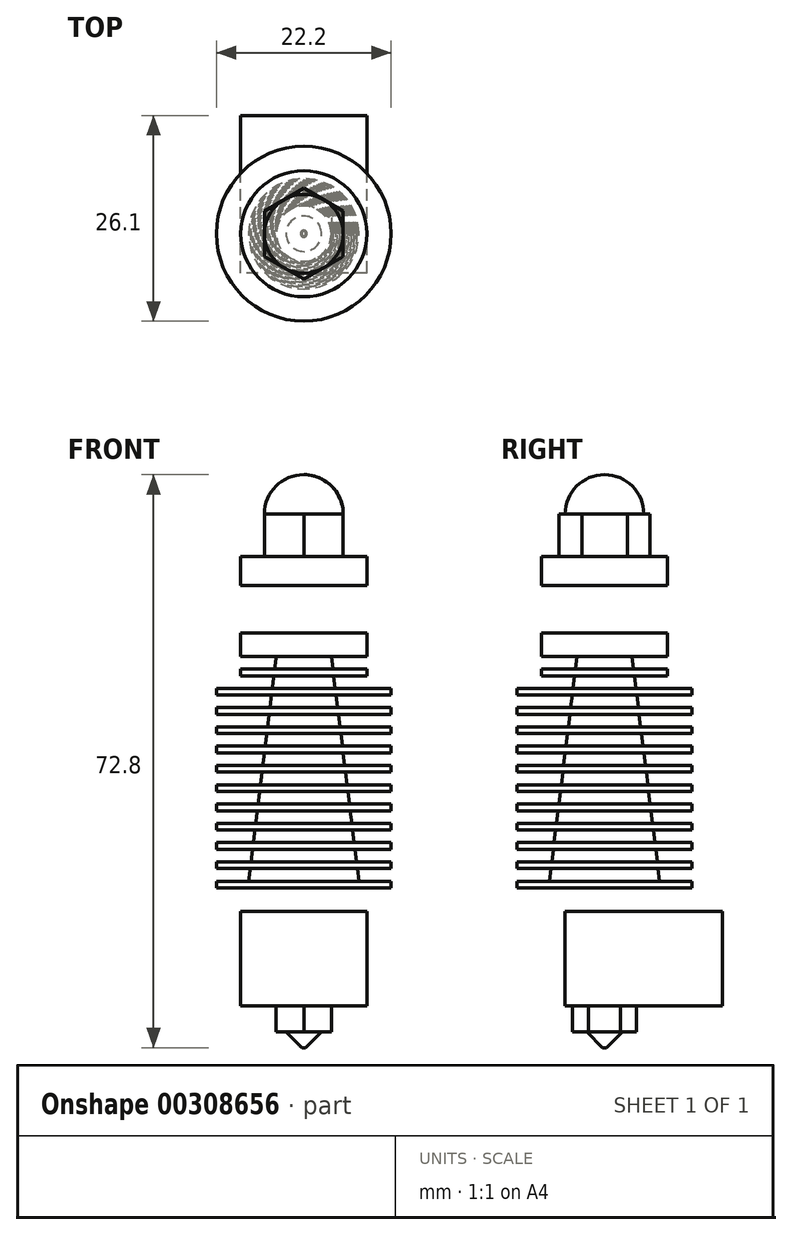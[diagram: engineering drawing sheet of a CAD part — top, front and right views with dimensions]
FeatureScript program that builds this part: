
annotation { "Feature Type Name" : "Feature", "Feature Type Description" : "" }
export const myFeature = defineFeature(function(context is Context, id is Id, definition is map)
    precondition{}
    {
        {
            var Q0;
            Q0=qCreatedBy(makeId("Front.planeOp"),FACE);
            var sketch = newSketch(context, id + "F0", { "sketchPlane" : qUnion([Q0])});
            skLineSegment(sketch, "E0.bottom", {"start": v(0, 0) * mm, "end": v(-11.1, 0) * mm});
            skLineSegment(sketch, "E0.top", {"start": v(0, -0.85) * mm, "end": v(-11.1, -0.85) * mm});
            skLineSegment(sketch, "E0.left", {"start": v(0, 0) * mm, "end": v(0, -0.85) * mm});
            skLineSegment(sketch, "E0.right", {"start": v(-11.1, 0) * mm, "end": v(-11.1, -0.85) * mm});
            skLineSegment(sketch, "E1.1.0.0", {"start": v(0, 1.6) * mm, "end": v(-11.1, 1.6) * mm});
            skLineSegment(sketch, "E1.1.0.1", {"start": v(-11.1, 2.45) * mm, "end": v(-11.1, 1.6) * mm});
            skLineSegment(sketch, "E1.1.0.2", {"start": v(0, 2.45) * mm, "end": v(-11.1, 2.45) * mm});
            skLineSegment(sketch, "E1.1.0.3", {"start": v(0, 2.45) * mm, "end": v(0, 1.6) * mm});
            skLineSegment(sketch, "E1.2.0.0", {"start": v(0, 4.05) * mm, "end": v(-11.1, 4.05) * mm});
            skLineSegment(sketch, "E1.2.0.1", {"start": v(-11.1, 4.9) * mm, "end": v(-11.1, 4.05) * mm});
            skLineSegment(sketch, "E1.2.0.2", {"start": v(0, 4.9) * mm, "end": v(-11.1, 4.9) * mm});
            skLineSegment(sketch, "E1.2.0.3", {"start": v(0, 4.9) * mm, "end": v(0, 4.05) * mm});
            skLineSegment(sketch, "E1.3.0.0", {"start": v(0, 6.5) * mm, "end": v(-11.1, 6.5) * mm});
            skLineSegment(sketch, "E1.3.0.1", {"start": v(-11.1, 7.35) * mm, "end": v(-11.1, 6.5) * mm});
            skLineSegment(sketch, "E1.3.0.2", {"start": v(0, 7.35) * mm, "end": v(-11.1, 7.35) * mm});
            skLineSegment(sketch, "E1.3.0.3", {"start": v(0, 7.35) * mm, "end": v(0, 6.5) * mm});
            skLineSegment(sketch, "E1.4.0.0", {"start": v(0, 8.95) * mm, "end": v(-11.1, 8.95) * mm});
            skLineSegment(sketch, "E1.4.0.1", {"start": v(-11.1, 9.8) * mm, "end": v(-11.1, 8.95) * mm});
            skLineSegment(sketch, "E1.4.0.2", {"start": v(0, 9.8) * mm, "end": v(-11.1, 9.8) * mm});
            skLineSegment(sketch, "E1.4.0.3", {"start": v(0, 9.8) * mm, "end": v(0, 8.95) * mm});
            skLineSegment(sketch, "E1.5.0.0", {"start": v(0, 11.4) * mm, "end": v(-11.1, 11.4) * mm});
            skLineSegment(sketch, "E1.5.0.1", {"start": v(-11.1, 12.25) * mm, "end": v(-11.1, 11.4) * mm});
            skLineSegment(sketch, "E1.5.0.2", {"start": v(0, 12.25) * mm, "end": v(-11.1, 12.25) * mm});
            skLineSegment(sketch, "E1.5.0.3", {"start": v(0, 12.25) * mm, "end": v(0, 11.4) * mm});
            skLineSegment(sketch, "E1.6.0.0", {"start": v(0, 13.85) * mm, "end": v(-11.1, 13.85) * mm});
            skLineSegment(sketch, "E1.6.0.1", {"start": v(-11.1, 14.7) * mm, "end": v(-11.1, 13.85) * mm});
            skLineSegment(sketch, "E1.6.0.2", {"start": v(0, 14.7) * mm, "end": v(-11.1, 14.7) * mm});
            skLineSegment(sketch, "E1.6.0.3", {"start": v(0, 14.7) * mm, "end": v(0, 13.85) * mm});
            skLineSegment(sketch, "E1.7.0.0", {"start": v(0, 16.3) * mm, "end": v(-11.1, 16.3) * mm});
            skLineSegment(sketch, "E1.7.0.1", {"start": v(-11.1, 17.15) * mm, "end": v(-11.1, 16.3) * mm});
            skLineSegment(sketch, "E1.7.0.2", {"start": v(0, 17.15) * mm, "end": v(-11.1, 17.15) * mm});
            skLineSegment(sketch, "E1.7.0.3", {"start": v(0, 17.15) * mm, "end": v(0, 16.3) * mm});
            skLineSegment(sketch, "E1.8.0.0", {"start": v(0, 18.75) * mm, "end": v(-11.1, 18.75) * mm});
            skLineSegment(sketch, "E1.8.0.1", {"start": v(-11.1, 19.6) * mm, "end": v(-11.1, 18.75) * mm});
            skLineSegment(sketch, "E1.8.0.2", {"start": v(0, 19.6) * mm, "end": v(-11.1, 19.6) * mm});
            skLineSegment(sketch, "E1.8.0.3", {"start": v(0, 19.6) * mm, "end": v(0, 18.75) * mm});
            skLineSegment(sketch, "E1.9.0.0", {"start": v(0, 21.2) * mm, "end": v(-11.1, 21.2) * mm});
            skLineSegment(sketch, "E1.9.0.1", {"start": v(-11.1, 22.05) * mm, "end": v(-11.1, 21.2) * mm});
            skLineSegment(sketch, "E1.9.0.2", {"start": v(0, 22.05) * mm, "end": v(-11.1, 22.05) * mm});
            skLineSegment(sketch, "E1.9.0.3", {"start": v(0, 22.05) * mm, "end": v(0, 21.2) * mm});
            skLineSegment(sketch, "E1.10.0.0", {"start": v(0, 23.65) * mm, "end": v(-11.1, 23.65) * mm});
            skLineSegment(sketch, "E1.10.0.1", {"start": v(-11.1, 24.5) * mm, "end": v(-11.1, 23.65) * mm});
            skLineSegment(sketch, "E1.10.0.2", {"start": v(0, 24.5) * mm, "end": v(-11.1, 24.5) * mm});
            skLineSegment(sketch, "E1.10.0.3", {"start": v(0, 24.5) * mm, "end": v(0, 23.65) * mm});
            skLineSegment(sketch, "E1.direction1", {"start": v(-11.1, -0.85) * mm, "end": v(-11.1, 1.6) * mm, "construction": true});
            skLineSegment(sketch, "E2.bottom", {"start": v(0, 26.95) * mm, "end": v(-8, 26.95) * mm});
            skLineSegment(sketch, "E2.top", {"start": v(0, 26.1) * mm, "end": v(-8, 26.1) * mm});
            skLineSegment(sketch, "E2.left", {"start": v(0, 26.95) * mm, "end": v(0, 26.1) * mm});
            skLineSegment(sketch, "E2.right", {"start": v(-8, 26.95) * mm, "end": v(-8, 26.1) * mm});
            skLineSegment(sketch, "E3.bottom", {"start": v(0, 31.55) * mm, "end": v(-8, 31.55) * mm});
            skLineSegment(sketch, "E3.top", {"start": v(0, 28.55) * mm, "end": v(-8, 28.55) * mm});
            skLineSegment(sketch, "E3.left", {"start": v(0, 31.55) * mm, "end": v(0, 28.55) * mm});
            skLineSegment(sketch, "E3.right", {"start": v(-8, 31.55) * mm, "end": v(-8, 28.55) * mm});
            skLineSegment(sketch, "E4.bottom", {"start": v(0, 31.55) * mm, "end": v(-6, 31.55) * mm});
            skLineSegment(sketch, "E4.top", {"start": v(0, 37.55) * mm, "end": v(-6, 37.55) * mm});
            skLineSegment(sketch, "E4.left", {"start": v(0, 31.55) * mm, "end": v(0, 37.55) * mm});
            skLineSegment(sketch, "E4.right", {"start": v(-6, 31.55) * mm, "end": v(-6, 37.55) * mm});
            skLineSegment(sketch, "E5.bottom", {"start": v(0, 37.55) * mm, "end": v(-8, 37.55) * mm});
            skLineSegment(sketch, "E5.top", {"start": v(0, 41.25) * mm, "end": v(-8, 41.25) * mm});
            skLineSegment(sketch, "E5.left", {"start": v(0, 37.55) * mm, "end": v(0, 41.25) * mm});
            skLineSegment(sketch, "E5.right", {"start": v(-8, 37.55) * mm, "end": v(-8, 41.25) * mm});
            skLineSegment(sketch, "E6", {"start": v(-3.5, 28.55) * mm, "end": v(-7, 0) * mm});
            skLineSegment(sketch, "E7", {"start": v(0, 28.55) * mm, "end": v(0, -0.85) * mm});
            skArc(sketch, "E8", {"start": v(-0.43, 31.55) * mm, "mid": v(-0.22, 31.5) * mm, "end": v(0, 31.45) * mm});
            skArc(sketch, "E9", {"start": v(0, 51.65) * mm, "mid": v(-3.54, 50.19) * mm, "end": v(-5, 46.65) * mm});
            skLineSegment(sketch, "E10", {"start": v(0, 46.65) * mm, "end": v(-5, 46.65) * mm});
            skLineSegment(sketch, "E11", {"start": v(0, 46.65) * mm, "end": v(0, 51.65) * mm});
            skLineSegment(sketch, "E12.bottom", {"start": v(0, -0.85) * mm, "end": v(-2.5, -0.85) * mm});
            skLineSegment(sketch, "E12.top", {"start": v(0, -3.85) * mm, "end": v(-2.5, -3.85) * mm});
            skLineSegment(sketch, "E12.left", {"start": v(0, -0.85) * mm, "end": v(0, -3.85) * mm});
            skLineSegment(sketch, "E12.right", {"start": v(-2.5, -0.85) * mm, "end": v(-2.5, -3.85) * mm});
            skLineSegment(sketch, "E13.bottom", {"start": v(0, -3.85) * mm, "end": v(-8, -3.85) * mm});
            skLineSegment(sketch, "E13.top", {"start": v(0, -15.85) * mm, "end": v(-8, -15.85) * mm});
            skLineSegment(sketch, "E13.left", {"start": v(0, -3.85) * mm, "end": v(0, -15.85) * mm});
            skLineSegment(sketch, "E13.right", {"start": v(-8, -3.85) * mm, "end": v(-8, -15.85) * mm});
            skLineSegment(sketch, "E14.MirrorCS", {"start": v(0, -15.85) * mm, "end": v(8, -15.85) * mm});
            skLineSegment(sketch, "E15.MirrorCS", {"start": v(8, -3.85) * mm, "end": v(8, -15.85) * mm});
            skLineSegment(sketch, "E16.MirrorCS", {"start": v(0, -3.85) * mm, "end": v(8, -3.85) * mm});
            skSolve(sketch);
        }
        {
            var Q0;
            Q0=makeQuery(id+"F0.imprint","IMPRINT",FACE,{"disambiguationData":[TD([[makeQuery(id+"F0.imprint","IMPRINT",EDGE,{"derivedFrom":sQuery(id+"F0.wireOp",EDGE,"E5.top")}),1.0]])]});
            var Q1;
            Q1=makeQuery(id+"F0.imprint","IMPRINT",FACE,{"disambiguationData":[TD([[makeQuery(id+"F0.imprint","IMPRINT",EDGE,{"derivedFrom":sQuery(id+"F0.wireOp",EDGE,"E4.bottom")}),-1.0]])]});
            var Q2;
            Q2=makeQuery(id+"F0.imprint","IMPRINT",FACE,{"disambiguationData":[TD([[makeQuery(id+"F0.imprint","IMPRINT",EDGE,{"derivedFrom":sQuery(id+"F0.wireOp",EDGE,"E3.bottom")}),1.0]])]});
            var Q3;
            {var subQ0=sQuery(id+"F0.wireOp",EDGE,"E7");var subQ1=sQuery(id+"F0.wireOp",EDGE,"E2.bottom");var subQ2=makeQuery(id+"F0.imprint","INTERSECT",VERTEX,{"derivedFrom":[subQ1,subQ0]});Q3=makeQuery(id+"F0.imprint","IMPRINT",FACE,{"disambiguationData":[TD([[makeQuery(id+"F0.imprint","IMPRINT",EDGE,{"disambiguationData":[TD([[subQ2,-1.0]])],"derivedFrom":subQ1}),-1.0]])]});}
            var Q4;
            {var subQ0=sQuery(id+"F0.wireOp",EDGE,"E7");var subQ1=sQuery(id+"F0.wireOp",EDGE,"E1.6.0.0");var subQ2=makeQuery(id+"F0.imprint","INTERSECT",VERTEX,{"derivedFrom":[subQ1,subQ0]});Q4=makeQuery(id+"F0.imprint","IMPRINT",FACE,{"disambiguationData":[TD([[makeQuery(id+"F0.imprint","IMPRINT",EDGE,{"disambiguationData":[TD([[subQ2,-1.0]])],"derivedFrom":subQ1}),-1.0]])]});}
            var Q5;
            {var subQ1=sQuery(id+"F0.wireOp",EDGE,"E0.top");Q5=makeQuery(id+"F0.imprint","IMPRINT",FACE,{"disambiguationData":[TD([[makeQuery(id+"F0.imprint","IMPRINT",EDGE,{"derivedFrom":subQ1}),-1.0]])]});}
            var Q6;
            {var subQ0=sQuery(id+"F0.wireOp",EDGE,"E7");var subQ1=sQuery(id+"F0.wireOp",EDGE,"E1.1.0.0");var subQ2=makeQuery(id+"F0.imprint","INTERSECT",VERTEX,{"derivedFrom":[subQ1,subQ0]});Q6=makeQuery(id+"F0.imprint","IMPRINT",FACE,{"disambiguationData":[TD([[makeQuery(id+"F0.imprint","IMPRINT",EDGE,{"disambiguationData":[TD([[subQ2,-1.0]])],"derivedFrom":subQ1}),-1.0]])]});}
            var Q7;
            {var subQ0=sQuery(id+"F0.wireOp",EDGE,"E7");var subQ1=sQuery(id+"F0.wireOp",EDGE,"E1.8.0.2");var subQ2=makeQuery(id+"F0.imprint","INTERSECT",VERTEX,{"derivedFrom":[subQ1,subQ0]});Q7=makeQuery(id+"F0.imprint","IMPRINT",FACE,{"disambiguationData":[TD([[makeQuery(id+"F0.imprint","IMPRINT",EDGE,{"disambiguationData":[TD([[subQ2,-1.0]])],"derivedFrom":subQ1}),-1.0]])]});}
            var Q8;
            {var subQ0=sQuery(id+"F0.wireOp",EDGE,"E7");var subQ1=sQuery(id+"F0.wireOp",EDGE,"E2.bottom");var subQ2=makeQuery(id+"F0.imprint","INTERSECT",VERTEX,{"derivedFrom":[subQ1,subQ0]});Q8=makeQuery(id+"F0.imprint","IMPRINT",FACE,{"disambiguationData":[TD([[makeQuery(id+"F0.imprint","IMPRINT",EDGE,{"disambiguationData":[TD([[subQ2,-1.0]])],"derivedFrom":subQ1}),1.0]])]});}
            var Q9;
            {var subQ0=sQuery(id+"F0.wireOp",EDGE,"E7");var subQ1=sQuery(id+"F0.wireOp",EDGE,"E1.4.0.0");var subQ2=makeQuery(id+"F0.imprint","INTERSECT",VERTEX,{"derivedFrom":[subQ1,subQ0]});Q9=makeQuery(id+"F0.imprint","IMPRINT",FACE,{"disambiguationData":[TD([[makeQuery(id+"F0.imprint","IMPRINT",EDGE,{"disambiguationData":[TD([[subQ2,-1.0]])],"derivedFrom":subQ1}),-1.0]])]});}
            var Q10;
            {var subQ0=sQuery(id+"F0.wireOp",EDGE,"E7");var subQ1=sQuery(id+"F0.wireOp",EDGE,"E1.2.0.0");var subQ2=makeQuery(id+"F0.imprint","INTERSECT",VERTEX,{"derivedFrom":[subQ1,subQ0]});Q10=makeQuery(id+"F0.imprint","IMPRINT",FACE,{"disambiguationData":[TD([[makeQuery(id+"F0.imprint","IMPRINT",EDGE,{"disambiguationData":[TD([[subQ2,-1.0]])],"derivedFrom":subQ1}),-1.0]])]});}
            var Q11;
            {var subQ0=sQuery(id+"F0.wireOp",EDGE,"E7");var subQ1=sQuery(id+"F0.wireOp",EDGE,"E1.10.0.2");var subQ2=makeQuery(id+"F0.imprint","INTERSECT",VERTEX,{"derivedFrom":[subQ1,subQ0]});Q11=makeQuery(id+"F0.imprint","IMPRINT",FACE,{"disambiguationData":[TD([[makeQuery(id+"F0.imprint","IMPRINT",EDGE,{"disambiguationData":[TD([[subQ2,-1.0]])],"derivedFrom":subQ1}),-1.0]])]});}
            var Q12;
            {var subQ0=sQuery(id+"F0.wireOp",EDGE,"E7");var subQ1=sQuery(id+"F0.wireOp",EDGE,"E1.4.0.2");var subQ2=makeQuery(id+"F0.imprint","INTERSECT",VERTEX,{"derivedFrom":[subQ1,subQ0]});Q12=makeQuery(id+"F0.imprint","IMPRINT",FACE,{"disambiguationData":[TD([[makeQuery(id+"F0.imprint","IMPRINT",EDGE,{"disambiguationData":[TD([[subQ2,-1.0]])],"derivedFrom":subQ1}),-1.0]])]});}
            var Q13;
            {var subQ0=sQuery(id+"F0.wireOp",EDGE,"E7");var subQ1=sQuery(id+"F0.wireOp",EDGE,"E1.7.0.0");var subQ2=makeQuery(id+"F0.imprint","INTERSECT",VERTEX,{"derivedFrom":[subQ1,subQ0]});Q13=makeQuery(id+"F0.imprint","IMPRINT",FACE,{"disambiguationData":[TD([[makeQuery(id+"F0.imprint","IMPRINT",EDGE,{"disambiguationData":[TD([[subQ2,-1.0]])],"derivedFrom":subQ1}),-1.0]])]});}
            var Q14;
            {var subQ0=sQuery(id+"F0.wireOp",EDGE,"E7");var subQ1=sQuery(id+"F0.wireOp",EDGE,"E1.10.0.0");var subQ2=makeQuery(id+"F0.imprint","INTERSECT",VERTEX,{"derivedFrom":[subQ1,subQ0]});Q14=makeQuery(id+"F0.imprint","IMPRINT",FACE,{"disambiguationData":[TD([[makeQuery(id+"F0.imprint","IMPRINT",EDGE,{"disambiguationData":[TD([[subQ2,-1.0]])],"derivedFrom":subQ1}),-1.0]])]});}
            var Q15;
            {var subQ0=sQuery(id+"F0.wireOp",EDGE,"E7");var subQ1=sQuery(id+"F0.wireOp",EDGE,"E1.3.0.0");var subQ2=makeQuery(id+"F0.imprint","INTERSECT",VERTEX,{"derivedFrom":[subQ1,subQ0]});Q15=makeQuery(id+"F0.imprint","IMPRINT",FACE,{"disambiguationData":[TD([[makeQuery(id+"F0.imprint","IMPRINT",EDGE,{"disambiguationData":[TD([[subQ2,-1.0]])],"derivedFrom":subQ1}),-1.0]])]});}
            var Q16;
            {var subQ0=sQuery(id+"F0.wireOp",EDGE,"E7");var subQ1=sQuery(id+"F0.wireOp",EDGE,"E1.3.0.2");var subQ2=makeQuery(id+"F0.imprint","INTERSECT",VERTEX,{"derivedFrom":[subQ1,subQ0]});Q16=makeQuery(id+"F0.imprint","IMPRINT",FACE,{"disambiguationData":[TD([[makeQuery(id+"F0.imprint","IMPRINT",EDGE,{"disambiguationData":[TD([[subQ2,-1.0]])],"derivedFrom":subQ1}),-1.0]])]});}
            var Q17;
            {var subQ0=sQuery(id+"F0.wireOp",EDGE,"E7");var subQ1=sQuery(id+"F0.wireOp",EDGE,"E1.1.0.2");var subQ2=makeQuery(id+"F0.imprint","INTERSECT",VERTEX,{"derivedFrom":[subQ1,subQ0]});Q17=makeQuery(id+"F0.imprint","IMPRINT",FACE,{"disambiguationData":[TD([[makeQuery(id+"F0.imprint","IMPRINT",EDGE,{"disambiguationData":[TD([[subQ2,-1.0]])],"derivedFrom":subQ1}),-1.0]])]});}
            var Q18;
            {var subQ0=sQuery(id+"F0.wireOp",EDGE,"E7");var subQ1=sQuery(id+"F0.wireOp",EDGE,"E0.bottom");var subQ2=makeQuery(id+"F0.imprint","INTERSECT",VERTEX,{"derivedFrom":[subQ1,subQ0]});Q18=makeQuery(id+"F0.imprint","IMPRINT",FACE,{"disambiguationData":[TD([[makeQuery(id+"F0.imprint","IMPRINT",EDGE,{"disambiguationData":[TD([[subQ2,-1.0]])],"derivedFrom":subQ1}),-1.0]])]});}
            var Q19;
            {var subQ0=sQuery(id+"F0.wireOp",EDGE,"E7");var subQ1=sQuery(id+"F0.wireOp",EDGE,"E1.2.0.2");var subQ2=makeQuery(id+"F0.imprint","INTERSECT",VERTEX,{"derivedFrom":[subQ1,subQ0]});Q19=makeQuery(id+"F0.imprint","IMPRINT",FACE,{"disambiguationData":[TD([[makeQuery(id+"F0.imprint","IMPRINT",EDGE,{"disambiguationData":[TD([[subQ2,-1.0]])],"derivedFrom":subQ1}),-1.0]])]});}
            var Q20;
            {var subQ0=sQuery(id+"F0.wireOp",EDGE,"E7");var subQ1=sQuery(id+"F0.wireOp",EDGE,"E1.7.0.2");var subQ2=makeQuery(id+"F0.imprint","INTERSECT",VERTEX,{"derivedFrom":[subQ1,subQ0]});Q20=makeQuery(id+"F0.imprint","IMPRINT",FACE,{"disambiguationData":[TD([[makeQuery(id+"F0.imprint","IMPRINT",EDGE,{"disambiguationData":[TD([[subQ2,-1.0]])],"derivedFrom":subQ1}),-1.0]])]});}
            var Q21;
            {var subQ0=sQuery(id+"F0.wireOp",EDGE,"E7");var subQ1=sQuery(id+"F0.wireOp",EDGE,"E1.9.0.2");var subQ2=makeQuery(id+"F0.imprint","INTERSECT",VERTEX,{"derivedFrom":[subQ1,subQ0]});Q21=makeQuery(id+"F0.imprint","IMPRINT",FACE,{"disambiguationData":[TD([[makeQuery(id+"F0.imprint","IMPRINT",EDGE,{"disambiguationData":[TD([[subQ2,-1.0]])],"derivedFrom":subQ1}),-1.0]])]});}
            var Q22;
            {var subQ0=sQuery(id+"F0.wireOp",EDGE,"E7");var subQ1=sQuery(id+"F0.wireOp",EDGE,"E1.5.0.2");var subQ2=makeQuery(id+"F0.imprint","INTERSECT",VERTEX,{"derivedFrom":[subQ1,subQ0]});Q22=makeQuery(id+"F0.imprint","IMPRINT",FACE,{"disambiguationData":[TD([[makeQuery(id+"F0.imprint","IMPRINT",EDGE,{"disambiguationData":[TD([[subQ2,-1.0]])],"derivedFrom":subQ1}),-1.0]])]});}
            var Q23;
            {var subQ0=sQuery(id+"F0.wireOp",EDGE,"E7");var subQ1=sQuery(id+"F0.wireOp",EDGE,"E1.8.0.0");var subQ2=makeQuery(id+"F0.imprint","INTERSECT",VERTEX,{"derivedFrom":[subQ1,subQ0]});Q23=makeQuery(id+"F0.imprint","IMPRINT",FACE,{"disambiguationData":[TD([[makeQuery(id+"F0.imprint","IMPRINT",EDGE,{"disambiguationData":[TD([[subQ2,-1.0]])],"derivedFrom":subQ1}),-1.0]])]});}
            var Q24;
            {var subQ0=sQuery(id+"F0.wireOp",EDGE,"E7");var subQ1=sQuery(id+"F0.wireOp",EDGE,"E1.9.0.0");var subQ2=makeQuery(id+"F0.imprint","INTERSECT",VERTEX,{"derivedFrom":[subQ1,subQ0]});Q24=makeQuery(id+"F0.imprint","IMPRINT",FACE,{"disambiguationData":[TD([[makeQuery(id+"F0.imprint","IMPRINT",EDGE,{"disambiguationData":[TD([[subQ2,-1.0]])],"derivedFrom":subQ1}),-1.0]])]});}
            var Q25;
            {var subQ0=sQuery(id+"F0.wireOp",EDGE,"E7");var subQ1=sQuery(id+"F0.wireOp",EDGE,"E1.6.0.2");var subQ2=makeQuery(id+"F0.imprint","INTERSECT",VERTEX,{"derivedFrom":[subQ1,subQ0]});Q25=makeQuery(id+"F0.imprint","IMPRINT",FACE,{"disambiguationData":[TD([[makeQuery(id+"F0.imprint","IMPRINT",EDGE,{"disambiguationData":[TD([[subQ2,-1.0]])],"derivedFrom":subQ1}),-1.0]])]});}
            var Q26;
            {var subQ0=sQuery(id+"F0.wireOp",EDGE,"E7");var subQ1=sQuery(id+"F0.wireOp",EDGE,"E1.5.0.0");var subQ2=makeQuery(id+"F0.imprint","INTERSECT",VERTEX,{"derivedFrom":[subQ1,subQ0]});Q26=makeQuery(id+"F0.imprint","IMPRINT",FACE,{"disambiguationData":[TD([[makeQuery(id+"F0.imprint","IMPRINT",EDGE,{"disambiguationData":[TD([[subQ2,-1.0]])],"derivedFrom":subQ1}),-1.0]])]});}
            var Q27;
            {var subQ0=sQuery(id+"F0.wireOp",EDGE,"E2.right");Q27=makeQuery(id+"F0.imprint","IMPRINT",FACE,{"disambiguationData":[TD([[makeQuery(id+"F0.imprint","IMPRINT",EDGE,{"derivedFrom":subQ0}),1.0]])]});}
            var Q28;
            {var subQ0=sQuery(id+"F0.wireOp",EDGE,"E1.10.0.1");Q28=makeQuery(id+"F0.imprint","IMPRINT",FACE,{"disambiguationData":[TD([[makeQuery(id+"F0.imprint","IMPRINT",EDGE,{"derivedFrom":subQ0}),1.0]])]});}
            var Q29;
            {var subQ0=sQuery(id+"F0.wireOp",EDGE,"E1.9.0.1");Q29=makeQuery(id+"F0.imprint","IMPRINT",FACE,{"disambiguationData":[TD([[makeQuery(id+"F0.imprint","IMPRINT",EDGE,{"derivedFrom":subQ0}),1.0]])]});}
            var Q30;
            {var subQ0=sQuery(id+"F0.wireOp",EDGE,"E1.8.0.1");Q30=makeQuery(id+"F0.imprint","IMPRINT",FACE,{"disambiguationData":[TD([[makeQuery(id+"F0.imprint","IMPRINT",EDGE,{"derivedFrom":subQ0}),1.0]])]});}
            var Q31;
            {var subQ0=sQuery(id+"F0.wireOp",EDGE,"E1.7.0.1");Q31=makeQuery(id+"F0.imprint","IMPRINT",FACE,{"disambiguationData":[TD([[makeQuery(id+"F0.imprint","IMPRINT",EDGE,{"derivedFrom":subQ0}),1.0]])]});}
            var Q32;
            {var subQ0=sQuery(id+"F0.wireOp",EDGE,"E1.6.0.1");Q32=makeQuery(id+"F0.imprint","IMPRINT",FACE,{"disambiguationData":[TD([[makeQuery(id+"F0.imprint","IMPRINT",EDGE,{"derivedFrom":subQ0}),1.0]])]});}
            var Q33;
            {var subQ0=sQuery(id+"F0.wireOp",EDGE,"E1.5.0.1");Q33=makeQuery(id+"F0.imprint","IMPRINT",FACE,{"disambiguationData":[TD([[makeQuery(id+"F0.imprint","IMPRINT",EDGE,{"derivedFrom":subQ0}),1.0]])]});}
            var Q34;
            {var subQ0=sQuery(id+"F0.wireOp",EDGE,"E1.4.0.1");Q34=makeQuery(id+"F0.imprint","IMPRINT",FACE,{"disambiguationData":[TD([[makeQuery(id+"F0.imprint","IMPRINT",EDGE,{"derivedFrom":subQ0}),1.0]])]});}
            var Q35;
            {var subQ0=sQuery(id+"F0.wireOp",EDGE,"E1.3.0.1");Q35=makeQuery(id+"F0.imprint","IMPRINT",FACE,{"disambiguationData":[TD([[makeQuery(id+"F0.imprint","IMPRINT",EDGE,{"derivedFrom":subQ0}),1.0]])]});}
            var Q36;
            {var subQ0=sQuery(id+"F0.wireOp",EDGE,"E1.2.0.1");Q36=makeQuery(id+"F0.imprint","IMPRINT",FACE,{"disambiguationData":[TD([[makeQuery(id+"F0.imprint","IMPRINT",EDGE,{"derivedFrom":subQ0}),1.0]])]});}
            var Q37;
            {var subQ0=sQuery(id+"F0.wireOp",EDGE,"E1.1.0.1");Q37=makeQuery(id+"F0.imprint","IMPRINT",FACE,{"disambiguationData":[TD([[makeQuery(id+"F0.imprint","IMPRINT",EDGE,{"derivedFrom":subQ0}),1.0]])]});}
            var Q38;
            Q38=makeQuery(id+"F0.imprint","IMPRINT",FACE,{"disambiguationData":[TD([[makeQuery(id+"F0.imprint","IMPRINT",EDGE,{"derivedFrom":sQuery(id+"F0.wireOp",EDGE,"E9")}),1.0]])]});
            var Q39;
            Q39=makeQuery(id+"F0.imprint","IMPRINT",FACE,{"disambiguationData":[TD([[makeQuery(id+"F0.imprint","IMPRINT",EDGE,{"derivedFrom":sQuery(id+"F0.wireOp",EDGE,"E12.bottom")}),1.0]])]});
            var Q40;
            Q40=sQuery(id+"F0.wireOp",EDGE,"E4.left");
            revolve(context, id + "F1", {"entities" : qUnion([Q0, Q1, Q2, Q3, Q4, Q5, Q6, Q7, Q8, Q9, Q10, Q11, Q12, Q13, Q14, Q15, Q16, Q17, Q18, Q19, Q20, Q21, Q22, Q23, Q24, Q25, Q26, Q27, Q28, Q29, Q30, Q31, Q32, Q33, Q34, Q35, Q36, Q37, Q38, Q39]), "axis" : qUnion([Q40]), "revolveType" : RevolveType.FULL});
        }
        {
            var Q0;
            Q0=qCreatedBy(makeId("Top.planeOp"),FACE);
            var sketch = newSketch(context, id + "F2", { "sketchPlane" : qUnion([Q0])});
            skCircle(sketch, "E17.cCircle", {"center": v(0, 0) * mm, "radius": 5 * mm, "construction": true});
            skLineSegment(sketch, "E17.0", {"start": v(5, 2.89) * mm, "end": v(5, -2.89) * mm});
            skLineSegment(sketch, "E17.1", {"start": v(5, -2.89) * mm, "end": v(0, -5.77) * mm});
            skLineSegment(sketch, "E17.2", {"start": v(0, -5.77) * mm, "end": v(-5, -2.89) * mm});
            skLineSegment(sketch, "E17.3", {"start": v(-5, -2.89) * mm, "end": v(-5, 2.89) * mm});
            skLineSegment(sketch, "E17.4", {"start": v(-5, 2.89) * mm, "end": v(0, 5.77) * mm});
            skLineSegment(sketch, "E17.5", {"start": v(0, 5.77) * mm, "end": v(5, 2.89) * mm});
            skPoint(sketch, "E17.0.midPoint", {"position": v(5, 0) * mm});
            skCircle(sketch, "E18", {"center": v(0, 0) * mm, "radius": 4 * mm});
            skSolve(sketch);
        }
        {
            var Q0;
            Q0=makeQuery(id+"F2.imprint","IMPRINT",FACE,{"disambiguationData":[TD([[makeQuery(id+"F2.imprint","IMPRINT",EDGE,{"derivedFrom":sQuery(id+"F2.wireOp",EDGE,"E17.0")}),-1.0]])]});
            var Q1;
            Q1=makeQuery(id+"F2.imprint","IMPRINT",FACE,{"disambiguationData":[TD([[makeQuery(id+"F2.imprint","IMPRINT",EDGE,{"derivedFrom":sQuery(id+"F2.wireOp",EDGE,"E18")}),1.0]])]});
            extrude(context, id + "F3", {"entities" : qUnion([Q0, Q1]), "depth" : 46.65 * mm, "hasSecondDirection" : true, "secondDirectionOppositeDirection" : false, "secondDirectionDepth" : 41.25 * mm});
        }
        {
            var Q0;
            Q0=makeQuery(id+"F0.imprint","IMPRINT",FACE,{"disambiguationData":[TD([[makeQuery(id+"F0.imprint","IMPRINT",EDGE,{"derivedFrom":sQuery(id+"F0.wireOp",EDGE,"E13.top")}),-1.0]])]});
            var Q1;
            Q1=makeQuery(id+"F0.imprint","IMPRINT",FACE,{"disambiguationData":[TD([[makeQuery(id+"F0.imprint","IMPRINT",EDGE,{"derivedFrom":sQuery(id+"F0.wireOp",EDGE,"E13.left")}),1.0]])]});
            extrude(context, id + "F4", {"entities" : qUnion([Q0, Q1]), "depth" : 5 * mm, "hasSecondDirection" : true, "secondDirectionOppositeDirection" : true, "secondDirectionDepth" : 15 * mm});
        }
        {
            var Q0;
            Q0=qCreatedBy(makeId("Top.planeOp"),FACE);
            var sketch = newSketch(context, id + "F5", { "sketchPlane" : qUnion([Q0])});
            skCircle(sketch, "E19.cCircle", {"center": v(0, 0) * mm, "radius": 3.5 * mm, "construction": true});
            skLineSegment(sketch, "E19.0", {"start": v(3.5, 2.02) * mm, "end": v(3.5, -2.02) * mm});
            skLineSegment(sketch, "E19.1", {"start": v(3.5, -2.02) * mm, "end": v(0, -4.04) * mm});
            skLineSegment(sketch, "E19.2", {"start": v(0, -4.04) * mm, "end": v(-3.5, -2.02) * mm});
            skLineSegment(sketch, "E19.3", {"start": v(-3.5, -2.02) * mm, "end": v(-3.5, 2.02) * mm});
            skLineSegment(sketch, "E19.4", {"start": v(-3.5, 2.02) * mm, "end": v(0, 4.04) * mm});
            skLineSegment(sketch, "E19.5", {"start": v(0, 4.04) * mm, "end": v(3.5, 2.02) * mm});
            skPoint(sketch, "E19.0.midPoint", {"position": v(3.5, 0) * mm});
            skCircle(sketch, "E20", {"center": v(0, 0) * mm, "radius": 2.25 * mm});
            skSolve(sketch);
        }
        {
            var Q0;
            Q0=makeQuery(id+"F5.imprint","IMPRINT",FACE,{"disambiguationData":[TD([[makeQuery(id+"F5.imprint","IMPRINT",EDGE,{"derivedFrom":sQuery(id+"F5.wireOp",EDGE,"E19.0")}),-1.0]])]});
            var Q1;
            Q1=makeQuery(id+"F5.imprint","IMPRINT",FACE,{"disambiguationData":[TD([[makeQuery(id+"F5.imprint","IMPRINT",EDGE,{"derivedFrom":sQuery(id+"F5.wireOp",EDGE,"E20")}),1.0]])]});
            extrude(context, id + "F6", {"entities" : qUnion([Q0, Q1]), "oppositeDirection" : true, "depth" : 19.15 * mm, "hasSecondDirection" : true, "secondDirectionOppositeDirection" : true, "secondDirectionDepth" : 15.85 * mm});
        }
        {
            var Q0;
            Q0=makeQuery(id+"F6.opExtrude","CAP_FACE",FACE,{"disambiguationData":[OSD([sQuery(id+"F5.wireOp",EDGE,"E19.0"),sQuery(id+"F5.wireOp",EDGE,"E19.1"),sQuery(id+"F5.wireOp",EDGE,"E19.2"),sQuery(id+"F5.wireOp",EDGE,"E19.3"),sQuery(id+"F5.wireOp",EDGE,"E19.4"),sQuery(id+"F5.wireOp",EDGE,"E19.5")])],"isStart":false});
            cPlane(context, id + "F7", {"entities" : qUnion([Q0]), "cplaneType" : CPlaneType.OFFSET, "offset" : 0 * mm, "oppositeDirection" : true, "width" : 150 * mm, "height" : 150 * mm});
        }
        {
            var Q0;
            Q0=qCreatedBy(id+"F7.planeOp",FACE);
            var sketch = newSketch(context, id + "F8", { "sketchPlane" : qUnion([Q0])});
            skCircle(sketch, "E21", {"center": v(0, 0) * mm, "radius": 2.25 * mm});
            skSolve(sketch);
        }
        {
            var Q0;
            Q0=makeQuery(id+"F8.imprint","IMPRINT",FACE,{"disambiguationData":[TD([[makeQuery(id+"F8.imprint","IMPRINT",EDGE,{"derivedFrom":sQuery(id+"F8.wireOp",EDGE,"E21")}),1.0]])]});
            extrude(context, id + "F9", {"entities" : qUnion([Q0]), "operationType" : NewBodyOperationType.ADD, "depth" : 2 * mm, "hasDraft" : true, "draftAngle" : 45 * degree, "draftPullDirection" : true});
        }
    });
